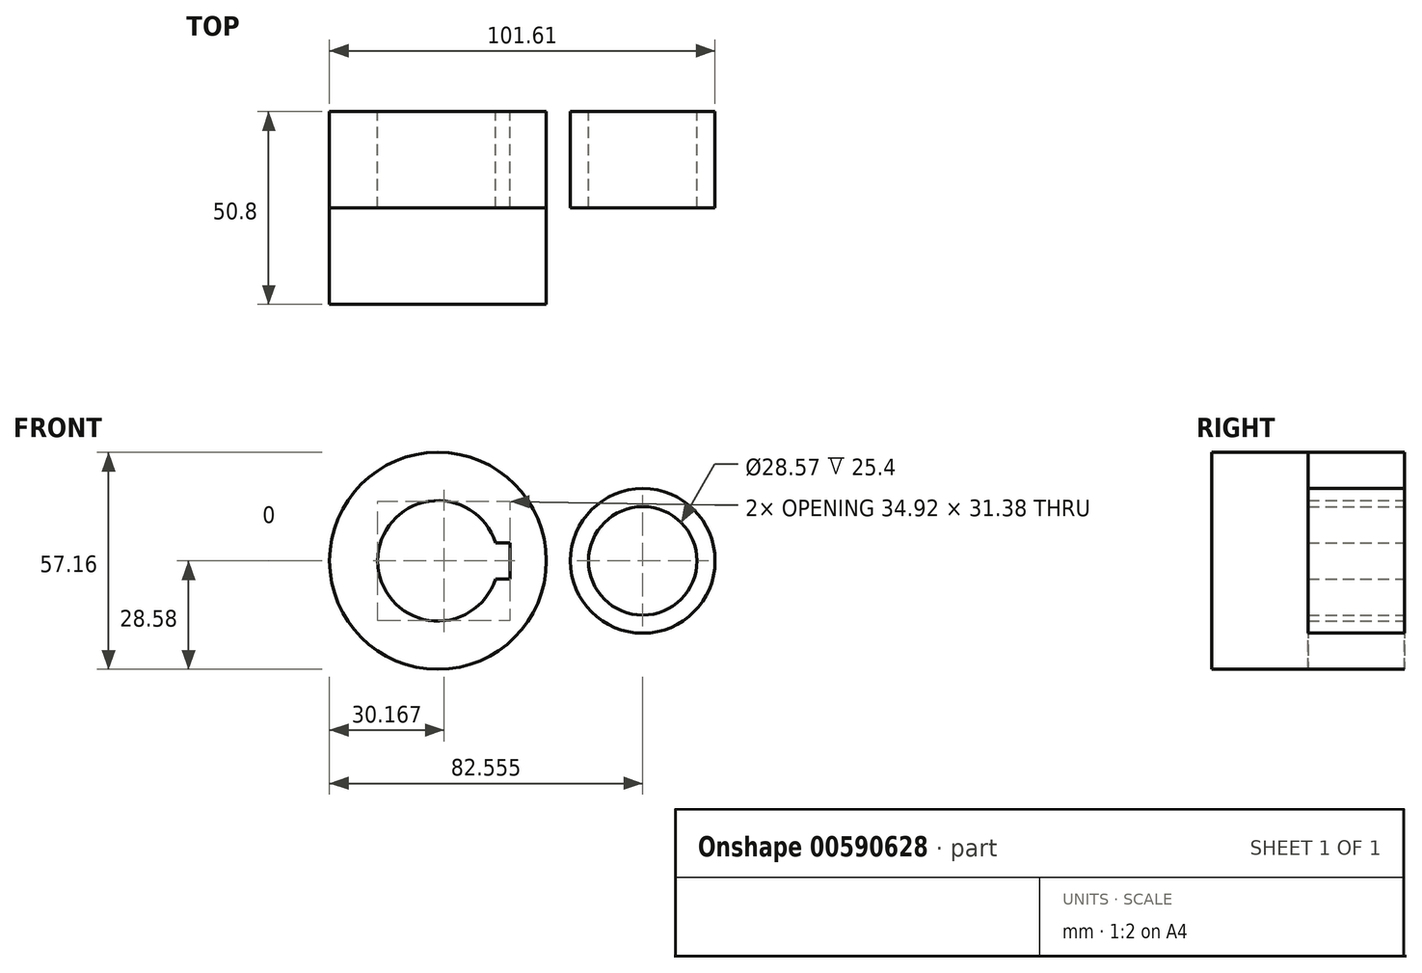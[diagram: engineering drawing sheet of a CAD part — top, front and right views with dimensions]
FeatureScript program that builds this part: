
annotation { "Feature Type Name" : "Feature", "Feature Type Description" : "" }
export const myFeature = defineFeature(function(context is Context, id is Id, definition is map)
    precondition{}
    {
        {
            var Q0;
            Q0=qCreatedBy(makeId("Front.planeOp"),FACE);
            var sketch = newSketch(context, id + "F0", { "sketchPlane" : qUnion([Q0])});
            skLineSegment(sketch, "E0", {"start": v(3.46, 28.4) * mm, "end": v(57.24, 18.77) * mm});
            skLineSegment(sketch, "E1", {"start": v(3.46, -28.4) * mm, "end": v(57.24, -18.77) * mm});
            skCircle(sketch, "E2", {"center": v(53.98, 0) * mm, "radius": 14.29 * mm});
            skCircle(sketch, "E3", {"center": v(0, 0) * mm, "radius": 28.58 * mm});
            skCircle(sketch, "E4", {"center": v(53.98, 0) * mm, "radius": 19.05 * mm});
            skCircle(sketch, "E5", {"center": v(0, 0) * mm, "radius": 15.88 * mm});
            skLineSegment(sketch, "E6.bottom", {"start": v(-19.05, 4.76) * mm, "end": v(19.05, 4.76) * mm});
            skLineSegment(sketch, "E6.top", {"start": v(-19.05, -4.76) * mm, "end": v(19.05, -4.76) * mm});
            skLineSegment(sketch, "E6.left", {"start": v(-19.05, 4.76) * mm, "end": v(-19.05, -4.76) * mm});
            skLineSegment(sketch, "E6.right", {"start": v(19.05, 4.76) * mm, "end": v(19.05, -4.76) * mm});
            skLineSegment(sketch, "E7", {"start": v(57.24, -18.77) * mm, "end": v(3.46, -28.4) * mm});
            skArc(sketch, "E8", {"start": v(3.46, -28.4) * mm, "mid": v(28.58, 0) * mm, "end": v(3.46, 28.4) * mm});
            skArc(sketch, "E9", {"start": v(57.24, 18.77) * mm, "mid": v(34.93, 0) * mm, "end": v(57.24, -18.77) * mm});
            skLineSegment(sketch, "E10", {"start": v(15.14, 4.76) * mm, "end": v(19.05, 4.76) * mm});
            skSolve(sketch);
        }
        {
            var Q0;
            {var subQ1=sQuery(id+"F0.wireOp",EDGE,"E6.left");Q0=makeQuery(id+"F0.imprint","IMPRINT",FACE,{"disambiguationData":[TD([[makeQuery(id+"F0.imprint","IMPRINT",EDGE,{"derivedFrom":subQ1}),-1.0]])]});}
            var Q1;
            {var subQ0=sQuery(id+"F0.wireOp",EDGE,"E6.left");Q1=makeQuery(id+"F0.imprint","IMPRINT",FACE,{"disambiguationData":[TD([[makeQuery(id+"F0.imprint","IMPRINT",EDGE,{"derivedFrom":subQ0}),1.0]])]});}
            var Q2;
            {var subQ1=sQuery(id+"F0.wireOp",EDGE,"E0");var subQ4=sQuery(id+"F0.wireOp",EDGE,"E9");var subQ8=makeQuery(id+"F0.imprint","INTERSECT",VERTEX,{"derivedFrom":[subQ1,subQ4]});Q2=makeQuery(id+"F0.imprint","IMPRINT",FACE,{"disambiguationData":[TD([[makeQuery(id+"F0.imprint","IMPRINT",EDGE,{"disambiguationData":[TD([[subQ8,1.0]])],"derivedFrom":subQ1}),-1.0]])]});}
            var Q3;
            Q3=makeQuery(id+"F0.imprint","IMPRINT",FACE,{"disambiguationData":[TD([[makeQuery(id+"F0.imprint","IMPRINT",EDGE,{"derivedFrom":sQuery(id+"F0.wireOp",EDGE,"E2")}),-1.0]])]});
            extrude(context, id + "F1", {"entities" : qUnion([Q0, Q1, Q2, Q3]), "depth" : 25.4 * mm, "offsetDistance" : 25.4 * mm});
        }
        {
            var Q0;
            Q0=makeQuery(id+"F1.opExtrude","CAP_FACE",FACE,{"disambiguationData":[OSD([sQuery(id+"F0.wireOp",EDGE,"E3"),sQuery(id+"F0.wireOp",EDGE,"E6.top"),sQuery(id+"F0.wireOp",EDGE,"E6.right"),sQuery(id+"F0.wireOp",EDGE,"E10"),sQuery(id+"F0.wireOp",EDGE,"E5")])],"isStart":true});
            extrude(context, id + "F2", {"entities" : qUnion([Q0]), "oppositeDirection" : true, "depth" : 50.8 * mm, "offsetDistance" : 25.4 * mm});
        }
    });
